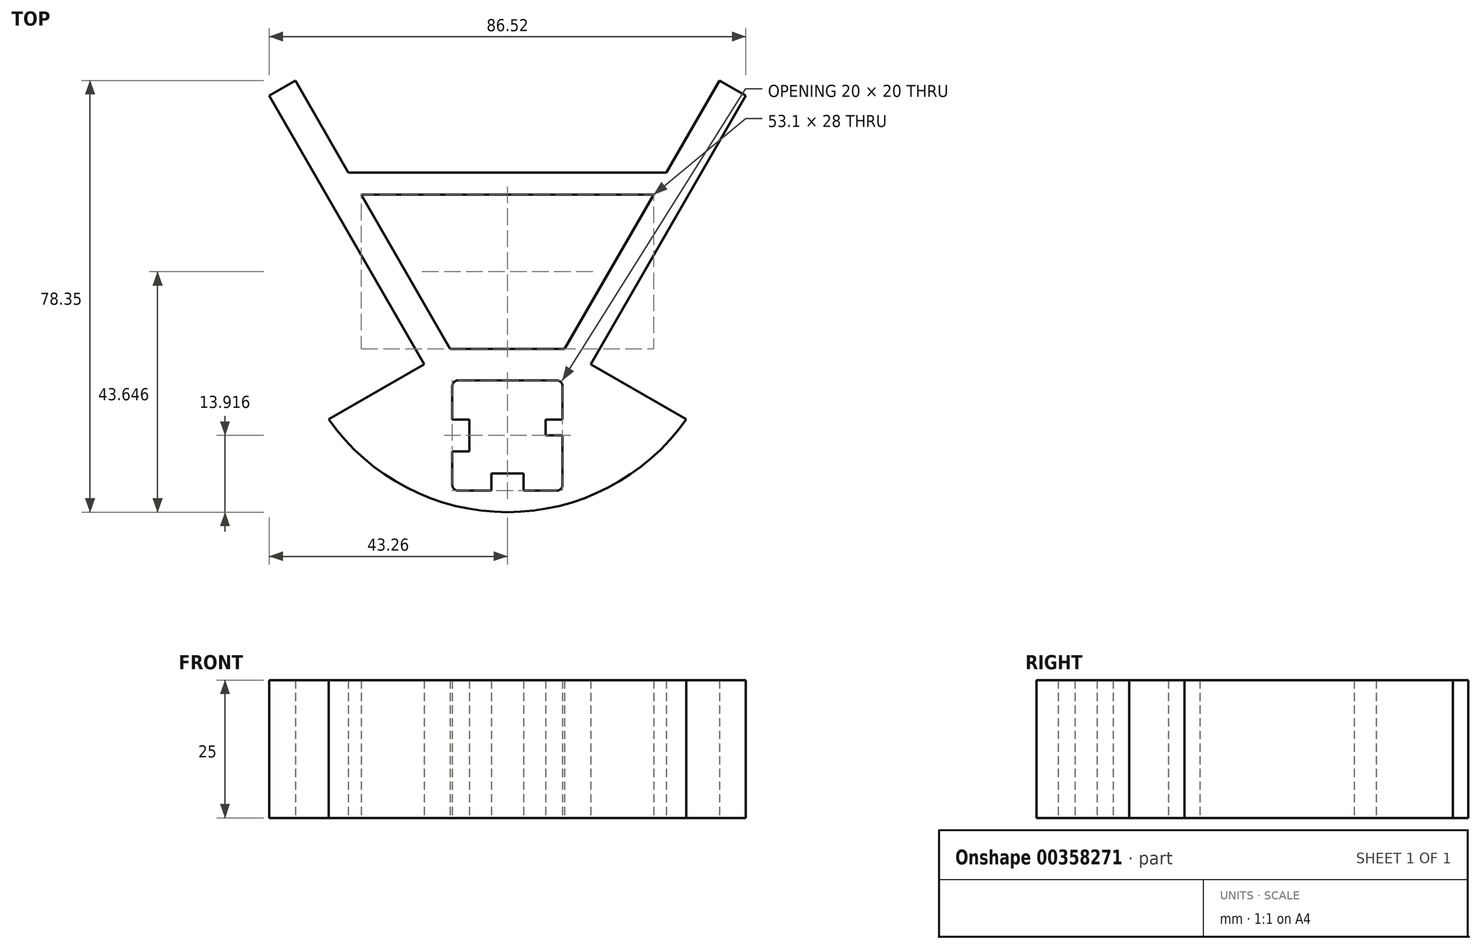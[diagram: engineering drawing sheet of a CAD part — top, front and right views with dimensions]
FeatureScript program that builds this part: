
annotation { "Feature Type Name" : "Feature", "Feature Type Description" : "" }
export const myFeature = defineFeature(function(context is Context, id is Id, definition is map)
    precondition{}
    {
        {
            var Q0;
            Q0=qCreatedBy(makeId("Top.planeOp"),FACE);
            var sketch = newSketch(context, id + "F0", { "sketchPlane" : qUnion([Q0])});
            skCircle(sketch, "E0", {"center": v(0, 22.42) * mm, "radius": 39.65 * mm});
            skLineSegment(sketch, "E1.bottom", {"start": v(10, -13.31) * mm, "end": v(-10, -13.31) * mm});
            skLineSegment(sketch, "E1.top", {"start": v(10, 6.69) * mm, "end": v(-10, 6.69) * mm});
            skLineSegment(sketch, "E1.left", {"start": v(10, -13.31) * mm, "end": v(10, 6.69) * mm});
            skLineSegment(sketch, "E1.right", {"start": v(-10, -13.31) * mm, "end": v(-10, 6.69) * mm});
            skPoint(sketch, "E1.middle", {"position": v(0, -3.31) * mm});
            skLineSegment(sketch, "E2", {"start": v(-32.44, -0.38) * mm, "end": v(32.44, -0.38) * mm});
            skLineSegment(sketch, "E3", {"start": v(32.44, -0.38) * mm, "end": v(60.58, 48.37) * mm});
            skLineSegment(sketch, "E4", {"start": v(-32.44, -0.38) * mm, "end": v(-60.58, 48.37) * mm});
            skLineSegment(sketch, "E5.0", {"start": v(-15.12, 9.62) * mm, "end": v(-43.26, 58.37) * mm});
            skLineSegment(sketch, "E6.0", {"start": v(15.12, 9.62) * mm, "end": v(43.26, 58.37) * mm});
            skLineSegment(sketch, "E7.0", {"start": v(10.36, 12.37) * mm, "end": v(38.5, 61.12) * mm});
            skLineSegment(sketch, "E8.0", {"start": v(-10.36, 12.37) * mm, "end": v(-38.5, 61.12) * mm});
            skLineSegment(sketch, "E9", {"start": v(-32.44, -0.38) * mm, "end": v(-10.36, 12.37) * mm});
            skLineSegment(sketch, "E10", {"start": v(32.44, -0.38) * mm, "end": v(10.36, 12.37) * mm});
            skLineSegment(sketch, "E11", {"start": v(-60.58, 48.37) * mm, "end": v(-38.5, 61.12) * mm});
            skLineSegment(sketch, "E12", {"start": v(60.58, 48.37) * mm, "end": v(38.5, 61.12) * mm});
            skLineSegment(sketch, "E13", {"start": v(-81.71, 12.42) * mm, "end": v(135.99, 12.42) * mm});
            skLineSegment(sketch, "E14.bottom", {"start": v(0, 6.69) * mm, "end": v(2.9, 6.69) * mm});
            skLineSegment(sketch, "E14.top", {"start": v(0, 3.59) * mm, "end": v(2.9, 3.59) * mm});
            skLineSegment(sketch, "E14.left", {"start": v(0, 6.69) * mm, "end": v(0, 3.59) * mm});
            skLineSegment(sketch, "E14.right", {"start": v(2.9, 6.69) * mm, "end": v(2.9, 3.59) * mm});
            skLineSegment(sketch, "E15.bottom", {"start": v(0, 6.69) * mm, "end": v(-2.9, 6.69) * mm});
            skLineSegment(sketch, "E15.top", {"start": v(0, 3.59) * mm, "end": v(-2.9, 3.59) * mm});
            skLineSegment(sketch, "E15.right", {"start": v(-2.9, 6.69) * mm, "end": v(-2.9, 3.59) * mm});
            skLineSegment(sketch, "E16", {"start": v(-10, -3.31) * mm, "end": v(10, -3.31) * mm});
            skLineSegment(sketch, "E17.MirrorCS", {"start": v(0, -10.21) * mm, "end": v(-2.9, -10.21) * mm});
            skLineSegment(sketch, "E18.MirrorCS", {"start": v(0, -10.21) * mm, "end": v(2.9, -10.21) * mm});
            skLineSegment(sketch, "E19.MirrorCS", {"start": v(2.9, -13.31) * mm, "end": v(2.9, -10.21) * mm});
            skLineSegment(sketch, "E20.MirrorCS", {"start": v(-2.9, -13.31) * mm, "end": v(-2.9, -10.21) * mm});
            skLineSegment(sketch, "E21.bottom", {"start": v(6.9, -3.31) * mm, "end": v(10, -3.31) * mm});
            skLineSegment(sketch, "E21.top", {"start": v(6.9, -0.41) * mm, "end": v(10, -0.41) * mm});
            skLineSegment(sketch, "E21.left", {"start": v(6.9, -3.31) * mm, "end": v(6.9, -0.41) * mm});
            skLineSegment(sketch, "E21.right", {"start": v(10, -3.31) * mm, "end": v(10, -0.41) * mm});
            skLineSegment(sketch, "E22.top", {"start": v(6.9, -6.21) * mm, "end": v(10, -6.21) * mm});
            skLineSegment(sketch, "E22.left", {"start": v(6.9, -3.31) * mm, "end": v(6.9, -6.21) * mm});
            skLineSegment(sketch, "E22.right", {"start": v(10, -3.31) * mm, "end": v(10, -6.21) * mm});
            skLineSegment(sketch, "E23", {"start": v(0, 6.69) * mm, "end": v(0, -13.31) * mm});
            skLineSegment(sketch, "E24.MirrorCS", {"start": v(-6.9, -6.21) * mm, "end": v(-10, -6.21) * mm});
            skLineSegment(sketch, "E25.MirrorCS", {"start": v(-6.9, -3.31) * mm, "end": v(-6.9, -6.21) * mm});
            skLineSegment(sketch, "E26.MirrorCS", {"start": v(-6.9, -3.31) * mm, "end": v(-6.9, -0.41) * mm});
            skLineSegment(sketch, "E27.MirrorCS", {"start": v(-6.9, -0.41) * mm, "end": v(-10, -0.41) * mm});
            skLineSegment(sketch, "E28", {"start": v(-108.15, 40.42) * mm, "end": v(133.1, 40.42) * mm});
            skLineSegment(sketch, "E29.0", {"start": v(-108.15, 44.42) * mm, "end": v(133.1, 44.42) * mm});
            skSolve(sketch);
        }
        {
            var Q0;
            {var subQ1=sQuery(id+"F0.wireOp",EDGE,"E1.bottom");Q0=makeQuery(id+"F0.imprint","IMPRINT",FACE,{"disambiguationData":[TD([[makeQuery(id+"F0.imprint","IMPRINT",EDGE,{"derivedFrom":subQ1}),1.0]])]});}
            var Q1;
            {var subQ0=sQuery(id+"F0.wireOp",EDGE,"E7.0");var subQ1=sQuery(id+"F0.wireOp",EDGE,"E0");var subQ2=makeQuery(id+"F0.imprint","INTERSECT",VERTEX,{"derivedFrom":[subQ1,subQ0]});Q1=makeQuery(id+"F0.imprint","IMPRINT",FACE,{"disambiguationData":[TD([[makeQuery(id+"F0.imprint","IMPRINT",EDGE,{"disambiguationData":[TD([[subQ2,1.0]])],"derivedFrom":subQ1}),1.0]])]});}
            var Q2;
            {var subQ0=sQuery(id+"F0.wireOp",EDGE,"E7.0");var subQ1=sQuery(id+"F0.wireOp",EDGE,"E0");var subQ2=makeQuery(id+"F0.imprint","INTERSECT",VERTEX,{"derivedFrom":[subQ1,subQ0]});Q2=makeQuery(id+"F0.imprint","IMPRINT",FACE,{"disambiguationData":[TD([[makeQuery(id+"F0.imprint","IMPRINT",EDGE,{"disambiguationData":[TD([[subQ2,1.0]])],"derivedFrom":subQ1}),-1.0]])]});}
            var Q3;
            {var subQ0=sQuery(id+"F0.wireOp",EDGE,"E8.0");var subQ1=sQuery(id+"F0.wireOp",EDGE,"E0");var subQ2=makeQuery(id+"F0.imprint","INTERSECT",VERTEX,{"derivedFrom":[subQ1,subQ0]});Q3=makeQuery(id+"F0.imprint","IMPRINT",FACE,{"disambiguationData":[TD([[makeQuery(id+"F0.imprint","IMPRINT",EDGE,{"disambiguationData":[TD([[subQ2,-1.0]])],"derivedFrom":subQ1}),-1.0]])]});}
            var Q4;
            {var subQ0=sQuery(id+"F0.wireOp",EDGE,"E8.0");var subQ1=sQuery(id+"F0.wireOp",EDGE,"E0");var subQ2=makeQuery(id+"F0.imprint","INTERSECT",VERTEX,{"derivedFrom":[subQ1,subQ0]});Q4=makeQuery(id+"F0.imprint","IMPRINT",FACE,{"disambiguationData":[TD([[makeQuery(id+"F0.imprint","IMPRINT",EDGE,{"disambiguationData":[TD([[subQ2,-1.0]])],"derivedFrom":subQ1}),1.0]])]});}
            var Q5;
            {var subQ13=sQuery(id+"F0.wireOp",EDGE,"E1.top");Q5=makeQuery(id+"F0.imprint","IMPRINT",FACE,{"disambiguationData":[TD([[makeQuery(id+"F0.imprint","IMPRINT",EDGE,{"derivedFrom":subQ13}),-1.0]])]});}
            var Q6;
            {var subQ0=sQuery(id+"F0.wireOp",EDGE,"E10");var subQ1=sQuery(id+"F0.wireOp",EDGE,"E6.0");var subQ2=makeQuery(id+"F0.imprint","INTERSECT",VERTEX,{"derivedFrom":[subQ1,subQ0]});Q6=makeQuery(id+"F0.imprint","IMPRINT",FACE,{"disambiguationData":[TD([[makeQuery(id+"F0.imprint","IMPRINT",EDGE,{"disambiguationData":[TD([[subQ2,-1.0]])],"derivedFrom":subQ1}),1.0]])]});}
            var Q7;
            {var subQ0=sQuery(id+"F0.wireOp",EDGE,"E9");var subQ1=sQuery(id+"F0.wireOp",EDGE,"E5.0");var subQ2=makeQuery(id+"F0.imprint","INTERSECT",VERTEX,{"derivedFrom":[subQ1,subQ0]});Q7=makeQuery(id+"F0.imprint","IMPRINT",FACE,{"disambiguationData":[TD([[makeQuery(id+"F0.imprint","IMPRINT",EDGE,{"disambiguationData":[TD([[subQ2,-1.0]])],"derivedFrom":subQ1}),-1.0]])]});}
            var Q8;
            {var subQ3=sQuery(id+"F0.wireOp",EDGE,"E24.MirrorCS");Q8=makeQuery(id+"F0.imprint","IMPRINT",FACE,{"disambiguationData":[TD([[makeQuery(id+"F0.imprint","IMPRINT",EDGE,{"derivedFrom":subQ3}),-1.0]])]});}
            var Q9;
            {var subQ4=sQuery(id+"F0.wireOp",EDGE,"E26.MirrorCS");Q9=makeQuery(id+"F0.imprint","IMPRINT",FACE,{"disambiguationData":[TD([[makeQuery(id+"F0.imprint","IMPRINT",EDGE,{"derivedFrom":subQ4}),1.0]])]});}
            var Q10;
            {var subQ0=sQuery(id+"F0.wireOp",EDGE,"E15.bottom");Q10=makeQuery(id+"F0.imprint","IMPRINT",FACE,{"disambiguationData":[TD([[makeQuery(id+"F0.imprint","IMPRINT",EDGE,{"derivedFrom":subQ0}),1.0]])]});}
            var Q11;
            {var subQ0=sQuery(id+"F0.wireOp",EDGE,"E14.bottom");Q11=makeQuery(id+"F0.imprint","IMPRINT",FACE,{"disambiguationData":[TD([[makeQuery(id+"F0.imprint","IMPRINT",EDGE,{"derivedFrom":subQ0}),-1.0]])]});}
            var Q12;
            Q12=makeQuery(id+"F0.imprint","IMPRINT",FACE,{"disambiguationData":[TD([[makeQuery(id+"F0.imprint","IMPRINT",EDGE,{"derivedFrom":sQuery(id+"F0.wireOp",EDGE,"E21.bottom")}),-1.0]])]});
            var Q13;
            Q13=makeQuery(id+"F0.imprint","IMPRINT",FACE,{"disambiguationData":[TD([[makeQuery(id+"F0.imprint","IMPRINT",EDGE,{"derivedFrom":sQuery(id+"F0.wireOp",EDGE,"E21.top")}),-1.0]])]});
            var Q14;
            {var subQ4=sQuery(id+"F0.wireOp",EDGE,"E18.MirrorCS");Q14=makeQuery(id+"F0.imprint","IMPRINT",FACE,{"disambiguationData":[TD([[makeQuery(id+"F0.imprint","IMPRINT",EDGE,{"derivedFrom":subQ4}),-1.0]])]});}
            var Q15;
            {var subQ4=sQuery(id+"F0.wireOp",EDGE,"E17.MirrorCS");Q15=makeQuery(id+"F0.imprint","IMPRINT",FACE,{"disambiguationData":[TD([[makeQuery(id+"F0.imprint","IMPRINT",EDGE,{"derivedFrom":subQ4}),1.0]])]});}
            var Q16;
            {var subQ0=sQuery(id+"F0.wireOp",EDGE,"E13");var subQ1=sQuery(id+"F0.wireOp",EDGE,"E5.0");var subQ2=makeQuery(id+"F0.imprint","INTERSECT",VERTEX,{"derivedFrom":[subQ1,subQ0]});Q16=makeQuery(id+"F0.imprint","IMPRINT",FACE,{"disambiguationData":[TD([[makeQuery(id+"F0.imprint","IMPRINT",EDGE,{"disambiguationData":[TD([[subQ2,-1.0]])],"derivedFrom":subQ1}),-1.0]])]});}
            var Q17;
            {var subQ0=sQuery(id+"F0.wireOp",EDGE,"E28");var subQ1=sQuery(id+"F0.wireOp",EDGE,"E7.0");var subQ2=makeQuery(id+"F0.imprint","INTERSECT",VERTEX,{"derivedFrom":[subQ1,subQ0]});Q17=makeQuery(id+"F0.imprint","IMPRINT",FACE,{"disambiguationData":[TD([[makeQuery(id+"F0.imprint","IMPRINT",EDGE,{"disambiguationData":[TD([[subQ2,-1.0]])],"derivedFrom":subQ1}),1.0]])]});}
            var Q18;
            {var subQ1=sQuery(id+"F0.wireOp",EDGE,"E6.0");var subQ7=sQuery(id+"F0.wireOp",EDGE,"E0");var subQ8=makeQuery(id+"F0.imprint","INTERSECT",VERTEX,{"derivedFrom":[subQ7,subQ1]});Q18=makeQuery(id+"F0.imprint","IMPRINT",FACE,{"disambiguationData":[TD([[makeQuery(id+"F0.imprint","IMPRINT",EDGE,{"disambiguationData":[TD([[subQ8,-1.0]])],"derivedFrom":subQ7}),1.0]])]});}
            var Q19;
            {var subQ0=sQuery(id+"F0.wireOp",EDGE,"E13");var subQ1=sQuery(id+"F0.wireOp",EDGE,"E6.0");var subQ2=makeQuery(id+"F0.imprint","INTERSECT",VERTEX,{"derivedFrom":[subQ1,subQ0]});Q19=makeQuery(id+"F0.imprint","IMPRINT",FACE,{"disambiguationData":[TD([[makeQuery(id+"F0.imprint","IMPRINT",EDGE,{"disambiguationData":[TD([[subQ2,-1.0]])],"derivedFrom":subQ1}),1.0]])]});}
            var Q20;
            {var subQ5=sQuery(id+"F0.wireOp",EDGE,"E29.0");var subQ7=sQuery(id+"F0.wireOp",EDGE,"E0");var subQ9=makeQuery(id+"F0.imprint","INTERSECT",VERTEX,{"disambiguationData":[OD(1.0)],"derivedFrom":[subQ7,subQ5]});Q20=makeQuery(id+"F0.imprint","IMPRINT",FACE,{"disambiguationData":[TD([[makeQuery(id+"F0.imprint","IMPRINT",EDGE,{"disambiguationData":[TD([[subQ9,-1.0]])],"derivedFrom":subQ7}),1.0]])]});}
            var Q21;
            {var subQ0=sQuery(id+"F0.wireOp",EDGE,"E29.0");var subQ1=sQuery(id+"F0.wireOp",EDGE,"E0");var subQ2=makeQuery(id+"F0.imprint","INTERSECT",VERTEX,{"disambiguationData":[OD(1.0)],"derivedFrom":[subQ1,subQ0]});Q21=makeQuery(id+"F0.imprint","IMPRINT",FACE,{"disambiguationData":[TD([[makeQuery(id+"F0.imprint","IMPRINT",EDGE,{"disambiguationData":[TD([[subQ2,-1.0]])],"derivedFrom":subQ1}),-1.0]])]});}
            var Q22;
            {var subQ0=sQuery(id+"F0.wireOp",EDGE,"E6.0");var subQ1=sQuery(id+"F0.wireOp",EDGE,"E0");var subQ2=makeQuery(id+"F0.imprint","INTERSECT",VERTEX,{"derivedFrom":[subQ1,subQ0]});Q22=makeQuery(id+"F0.imprint","IMPRINT",FACE,{"disambiguationData":[TD([[makeQuery(id+"F0.imprint","IMPRINT",EDGE,{"disambiguationData":[TD([[subQ2,-1.0]])],"derivedFrom":subQ1}),-1.0]])]});}
            extrude(context, id + "F1", {"entities" : qUnion([Q0, Q1, Q2, Q3, Q4, Q5, Q6, Q7, Q8, Q9, Q10, Q11, Q12, Q13, Q14, Q15, Q16, Q17, Q18, Q19, Q20, Q21, Q22]), "depth" : 25 * mm});
        }
        {
            var Q0;
            Q0=makeQuery(id+"F1.opExtrude","SWEPT_EDGE",EDGE,{"disambiguationData":[OSD([sQuery(id+"F0.wireOp",EDGE,"E1.bottom"),sQuery(id+"F0.wireOp",EDGE,"E1.right")])]});
            var Q1;
            Q1=makeQuery(id+"F1.opExtrude","SWEPT_EDGE",EDGE,{"disambiguationData":[OSD([sQuery(id+"F0.wireOp",EDGE,"E1.top"),sQuery(id+"F0.wireOp",EDGE,"E1.right")])]});
            var Q2;
            Q2=makeQuery(id+"F1.opExtrude","SWEPT_EDGE",EDGE,{"disambiguationData":[OSD([sQuery(id+"F0.wireOp",EDGE,"E1.bottom"),sQuery(id+"F0.wireOp",EDGE,"E1.left")])]});
            var Q3;
            Q3=makeQuery(id+"F1.opExtrude","SWEPT_EDGE",EDGE,{"disambiguationData":[OSD([sQuery(id+"F0.wireOp",EDGE,"E1.top"),sQuery(id+"F0.wireOp",EDGE,"E1.left")])]});
            fillet(context, id + "F2", {"entities" : qUnion([Q0, Q1, Q2, Q3]), "radius" : 1 * mm, "tangentPropagation" : true, "allowEdgeOverflow" : false});
        }
    });
